# Revit family: RN 26030 Rubinetto a sfera
name_source: partatom
category: Rohrzubehör
units: mm (PartAtom-declared; Revit-internal decimal feet)

## family parameters
Arbeitsebenenbasiert = Nein
Beim Laden mit Abzugskörper schneiden = Nein
Bemaßung runder Anschluss = Durchmesser verwenden
Gemeinsam genutzt = Nein
Immer vertikal = Ja
Teiletyp = Ventil - Zerlegung in

## types (9) — shared parameters
1.010.00.2 Number of the part of the guideline = 2
1.010.00.3 Issue date (month) of the guideline = 201601
1.010.00.4 Manufacturer name = R. Nussbaum AG
1.010.00.5 Revision date of the file = 20190514
1.100.00.3 Sort number for display sequence = 4
1.100.00.4 Product designation = Absperr- und Regelarmaturen
1.960/3L.00.8 Link (URL) = https://www.nussbaum.ch
2.700.00.4 valve assembly type = 11
2.700.00.7 maximum operating temperature TB [°C] = 100
2.700.00.8 maximum operating pressure(working pressure) ps [1.0 · 102 Pa] = 16
Connector Visibility = Nein
EnclosingSpace Visibility = Nein
Hersteller = R. Nussbauzm AG
Modell = 0
URL = https://www.nussbaum.ch

## per-type parameters (varying)
- DN 8: 1.800.00.3 BS number=0040160000000000000000000000090070000000000000000100000000; 1.810.00.3 Manufacturer’s reference number=26030.62; 1.810.00.4 DATANORM number=26030.62; 1.810.00.5 StLB number=655.131; 1.810.00.6 GTIN number=7612945704214; 2.700.00.26 product description=26030.62, Kugelhahn, Edelstahl, DN=8, Rp=¼; 2.700.00.5 nominal size DN=8; 2.700.00.6 kvs-value [m3/h]=8; CONNECTOR0_DIAMETER_dX_0r=8 mm  [stored 0.0262467 ft]; CONNECTOR0_dX_00=20 mm; CONNECTOR0_dX_01=10 mm  [stored 0.0328084 ft]; CONNECTOR0_ref_dX=10 mm  [stored 0.0328084 ft]; CONNECTOR1_DIAMETER_dX_0r=8 mm  [stored 0.0262467 ft]; CONNECTOR1_dX_00=10 mm  [stored 0.0328084 ft]; CONNECTOR1_dX_01=20 mm; CONNECTOR1_ref_dX=10 mm  [stored 0.0328084 ft]; R. Nussbaum AG 26030.62 en Visibility=Ja; R. Nussbaum AG 26030.63 en Visibility=Nein; R. Nussbaum AG 26030.64 en Visibility=Nein; R. Nussbaum AG 26030.65 en Visibility=Nein; R. Nussbaum AG 26030.66 en Visibility=Nein; R. Nussbaum AG 26030.67 en Visibility=Nein; R. Nussbaum AG 26030.68 en Visibility=Nein; R. Nussbaum AG 26030.69 en Visibility=Nein; R. Nussbaum AG 26030.70 en Visibility=Nein; Typenkommentare=Valvola d'arrestoDN 8
- DN 10: 1.800.00.3 BS number=0040160000000000000000000000090070000000000000000200000000; 1.810.00.3 Manufacturer’s reference number=26030.63; 1.810.00.4 DATANORM number=26030.63; 1.810.00.5 StLB number=655.132; 1.810.00.6 GTIN number=7612945704221; 2.700.00.26 product description=26030.63, Kugelhahn, Edelstahl, DN=10, Rp=3/8; 2.700.00.5 nominal size DN=10; 2.700.00.6 kvs-value [m3/h]=10.3; CONNECTOR0_DIAMETER_dX_0r=10 mm  [stored 0.0328084 ft]; CONNECTOR0_dX_00=21 mm  [stored 0.0688976 ft]; CONNECTOR0_dX_01=11 mm; CONNECTOR0_ref_dX=11 mm; CONNECTOR1_DIAMETER_dX_0r=10 mm  [stored 0.0328084 ft]; CONNECTOR1_dX_00=11 mm; CONNECTOR1_dX_01=21 mm  [stored 0.0688976 ft]; CONNECTOR1_ref_dX=11 mm; R. Nussbaum AG 26030.62 en Visibility=Nein; R. Nussbaum AG 26030.63 en Visibility=Ja; R. Nussbaum AG 26030.64 en Visibility=Nein; R. Nussbaum AG 26030.65 en Visibility=Nein; R. Nussbaum AG 26030.66 en Visibility=Nein; R. Nussbaum AG 26030.67 en Visibility=Nein; R. Nussbaum AG 26030.68 en Visibility=Nein; R. Nussbaum AG 26030.69 en Visibility=Nein; R. Nussbaum AG 26030.70 en Visibility=Nein; Typenkommentare=Valvola d'arrestoDN 10
- DN 15: 1.800.00.3 BS number=0040160000000000000000000000090070000000000000000300000000; 1.810.00.3 Manufacturer’s reference number=26030.64; 1.810.00.4 DATANORM number=26030.64; 1.810.00.5 StLB number=655.133; 1.810.00.6 GTIN number=7612945704238; 2.700.00.26 product description=26030.64, Kugelhahn, Edelstahl, DN=15, Rp=½; 2.700.00.5 nominal size DN=15; 2.700.00.6 kvs-value [m3/h]=35; CONNECTOR0_DIAMETER_dX_0r=15 mm; CONNECTOR0_dX_00=25 mm  [stored 0.082021 ft]; CONNECTOR0_dX_01=12 mm  [stored 0.0393701 ft]; CONNECTOR0_ref_dX=12 mm  [stored 0.0393701 ft]; CONNECTOR1_DIAMETER_dX_0r=15 mm; CONNECTOR1_dX_00=12 mm  [stored 0.0393701 ft]; CONNECTOR1_dX_01=25 mm  [stored 0.082021 ft]; CONNECTOR1_ref_dX=12 mm  [stored 0.0393701 ft]; R. Nussbaum AG 26030.62 en Visibility=Nein; R. Nussbaum AG 26030.63 en Visibility=Nein; R. Nussbaum AG 26030.64 en Visibility=Ja; R. Nussbaum AG 26030.65 en Visibility=Nein; R. Nussbaum AG 26030.66 en Visibility=Nein; R. Nussbaum AG 26030.67 en Visibility=Nein; R. Nussbaum AG 26030.68 en Visibility=Nein; R. Nussbaum AG 26030.69 en Visibility=Nein; R. Nussbaum AG 26030.70 en Visibility=Nein; Typenkommentare=Valvola d'arrestoDN 15
- DN 20: 1.800.00.3 BS number=0040160000000000000000000000090070000000000000000400000000; 1.810.00.3 Manufacturer’s reference number=26030.65; 1.810.00.4 DATANORM number=26030.65; 1.810.00.5 StLB number=655.134; 1.810.00.6 GTIN number=7612945704245; 2.700.00.26 product description=26030.65, Kugelhahn, Edelstahl, DN=20, Rp=¾; 2.700.00.5 nominal size DN=20; 2.700.00.6 kvs-value [m3/h]=47; CONNECTOR0_DIAMETER_dX_0r=20 mm; CONNECTOR0_dX_00=30 mm; CONNECTOR0_dX_01=15 mm; CONNECTOR0_ref_dX=15 mm; CONNECTOR1_DIAMETER_dX_0r=20 mm; CONNECTOR1_dX_00=15 mm; CONNECTOR1_dX_01=30 mm; CONNECTOR1_ref_dX=15 mm; R. Nussbaum AG 26030.62 en Visibility=Nein; R. Nussbaum AG 26030.63 en Visibility=Nein; R. Nussbaum AG 26030.64 en Visibility=Nein; R. Nussbaum AG 26030.65 en Visibility=Ja; R. Nussbaum AG 26030.66 en Visibility=Nein; R. Nussbaum AG 26030.67 en Visibility=Nein; R. Nussbaum AG 26030.68 en Visibility=Nein; R. Nussbaum AG 26030.69 en Visibility=Nein; R. Nussbaum AG 26030.70 en Visibility=Nein; Typenkommentare=Valvola d'arrestoDN 20
- DN 25: 1.800.00.3 BS number=0040160000000000000000000000090070000000000000000500000000; 1.810.00.3 Manufacturer’s reference number=26030.66; 1.810.00.4 DATANORM number=26030.66; 1.810.00.5 StLB number=655.135; 1.810.00.6 GTIN number=7612945704252; 2.700.00.26 product description=26030.66, Kugelhahn, Edelstahl, DN=25, Rp=1; 2.700.00.5 nominal size DN=25; 2.700.00.6 kvs-value [m3/h]=54; CONNECTOR0_DIAMETER_dX_0r=25 mm  [stored 0.082021 ft]; CONNECTOR0_dX_00=34 mm; CONNECTOR0_dX_01=17 mm; CONNECTOR0_ref_dX=17 mm; CONNECTOR1_DIAMETER_dX_0r=25 mm  [stored 0.082021 ft]; CONNECTOR1_dX_00=17 mm; CONNECTOR1_dX_01=34 mm; CONNECTOR1_ref_dX=17 mm; R. Nussbaum AG 26030.62 en Visibility=Nein; R. Nussbaum AG 26030.63 en Visibility=Nein; R. Nussbaum AG 26030.64 en Visibility=Nein; R. Nussbaum AG 26030.65 en Visibility=Nein; R. Nussbaum AG 26030.66 en Visibility=Ja; R. Nussbaum AG 26030.67 en Visibility=Nein; R. Nussbaum AG 26030.68 en Visibility=Nein; R. Nussbaum AG 26030.69 en Visibility=Nein; R. Nussbaum AG 26030.70 en Visibility=Nein; Typenkommentare=Valvola d'arrestoDN 25
- DN 32: 1.800.00.3 BS number=0040160000000000000000000000090070000000000000000600000000; 1.810.00.3 Manufacturer’s reference number=26030.67; 1.810.00.4 DATANORM number=26030.67; 1.810.00.5 StLB number=655.136; 1.810.00.6 GTIN number=7612945704269; 2.700.00.26 product description=26030.67, Kugelhahn, Edelstahl, DN=32, Rp=1¼; 2.700.00.5 nominal size DN=32; 2.700.00.6 kvs-value [m3/h]=82; CONNECTOR0_DIAMETER_dX_0r=32 mm; CONNECTOR0_dX_00=43 mm; CONNECTOR0_dX_01=24 mm  [stored 0.0787402 ft]; CONNECTOR0_ref_dX=24 mm  [stored 0.0787402 ft]; CONNECTOR1_DIAMETER_dX_0r=32 mm; CONNECTOR1_dX_00=24 mm  [stored 0.0787402 ft]; CONNECTOR1_dX_01=43 mm; CONNECTOR1_ref_dX=24 mm  [stored 0.0787402 ft]; R. Nussbaum AG 26030.62 en Visibility=Nein; R. Nussbaum AG 26030.63 en Visibility=Nein; R. Nussbaum AG 26030.64 en Visibility=Nein; R. Nussbaum AG 26030.65 en Visibility=Nein; R. Nussbaum AG 26030.66 en Visibility=Nein; R. Nussbaum AG 26030.67 en Visibility=Ja; R. Nussbaum AG 26030.68 en Visibility=Nein; R. Nussbaum AG 26030.69 en Visibility=Nein; R. Nussbaum AG 26030.70 en Visibility=Nein; Typenkommentare=Valvola d'arrestoDN 32
- DN 40: 1.800.00.3 BS number=0040160000000000000000000000090070000000000000000700000000; 1.810.00.3 Manufacturer’s reference number=26030.68; 1.810.00.4 DATANORM number=26030.68; 1.810.00.5 StLB number=655.137; 1.810.00.6 GTIN number=7612945704276; 2.700.00.26 product description=26030.68, Kugelhahn, Edelstahl, DN=40, Rp=1½; 2.700.00.5 nominal size DN=40; 2.700.00.6 kvs-value [m3/h]=160; CONNECTOR0_DIAMETER_dX_0r=40 mm; CONNECTOR0_dX_00=45 mm; CONNECTOR0_dX_01=26 mm; CONNECTOR0_ref_dX=26 mm; CONNECTOR1_DIAMETER_dX_0r=40 mm; CONNECTOR1_dX_00=26 mm; CONNECTOR1_dX_01=45 mm; CONNECTOR1_ref_dX=26 mm; R. Nussbaum AG 26030.62 en Visibility=Nein; R. Nussbaum AG 26030.63 en Visibility=Nein; R. Nussbaum AG 26030.64 en Visibility=Nein; R. Nussbaum AG 26030.65 en Visibility=Nein; R. Nussbaum AG 26030.66 en Visibility=Nein; R. Nussbaum AG 26030.67 en Visibility=Nein; R. Nussbaum AG 26030.68 en Visibility=Ja; R. Nussbaum AG 26030.69 en Visibility=Nein; R. Nussbaum AG 26030.70 en Visibility=Nein; Typenkommentare=Valvola d'arrestoDN 40
- DN 50: 1.800.00.3 BS number=0040160000000000000000000000090070000000000000000800000000; 1.810.00.3 Manufacturer’s reference number=26030.69; 1.810.00.4 DATANORM number=26030.69; 1.810.00.5 StLB number=655.138; 1.810.00.6 GTIN number=7612945704283; 2.700.00.26 product description=26030.69, Kugelhahn, Edelstahl, DN=50, Rp=2; 2.700.00.5 nominal size DN=50; 2.700.00.6 kvs-value [m3/h]=230; CONNECTOR0_DIAMETER_dX_0r=50 mm; CONNECTOR0_dX_00=53 mm; CONNECTOR0_dX_01=29 mm; CONNECTOR0_ref_dX=29 mm; CONNECTOR1_DIAMETER_dX_0r=50 mm; CONNECTOR1_dX_00=29 mm; CONNECTOR1_dX_01=53 mm; CONNECTOR1_ref_dX=29 mm; R. Nussbaum AG 26030.62 en Visibility=Nein; R. Nussbaum AG 26030.63 en Visibility=Nein; R. Nussbaum AG 26030.64 en Visibility=Nein; R. Nussbaum AG 26030.65 en Visibility=Nein; R. Nussbaum AG 26030.66 en Visibility=Nein; R. Nussbaum AG 26030.67 en Visibility=Nein; R. Nussbaum AG 26030.68 en Visibility=Nein; R. Nussbaum AG 26030.69 en Visibility=Ja; R. Nussbaum AG 26030.70 en Visibility=Nein; Typenkommentare=Valvola d'arrestoDN 50
- DN 65: 1.800.00.3 BS number=0040160000000000000000000000090070000000000000000900000000; 1.810.00.3 Manufacturer’s reference number=26030.70; 1.810.00.4 DATANORM number=26030.70; 1.810.00.5 StLB number=655.138; 1.810.00.6 GTIN number=7612945704290; 2.700.00.26 product description=26030.70, Kugelhahn, Edelstahl, DN=65, Rp=2½; 2.700.00.5 nominal size DN=65; 2.700.00.6 kvs-value [m3/h]=510; CONNECTOR0_DIAMETER_dX_0r=65 mm; CONNECTOR0_dX_00=70 mm; CONNECTOR0_dX_01=43 mm; CONNECTOR0_ref_dX=43 mm; CONNECTOR1_DIAMETER_dX_0r=65 mm; CONNECTOR1_dX_00=43 mm; CONNECTOR1_dX_01=70 mm; CONNECTOR1_ref_dX=43 mm; R. Nussbaum AG 26030.62 en Visibility=Nein; R. Nussbaum AG 26030.63 en Visibility=Nein; R. Nussbaum AG 26030.64 en Visibility=Nein; R. Nussbaum AG 26030.65 en Visibility=Nein; R. Nussbaum AG 26030.66 en Visibility=Nein; R. Nussbaum AG 26030.67 en Visibility=Nein; R. Nussbaum AG 26030.68 en Visibility=Nein; R. Nussbaum AG 26030.69 en Visibility=Nein; R. Nussbaum AG 26030.70 en Visibility=Ja; Typenkommentare=Valvola d'arrestoDN 65

note: [stored X ft] marks values corroborated as IEEE doubles in the binary element streams (Revit-internal decimal feet)

## geometry (parser evidence)
native form markers: Sweep x1
no freeform markers — native parametric forms only
